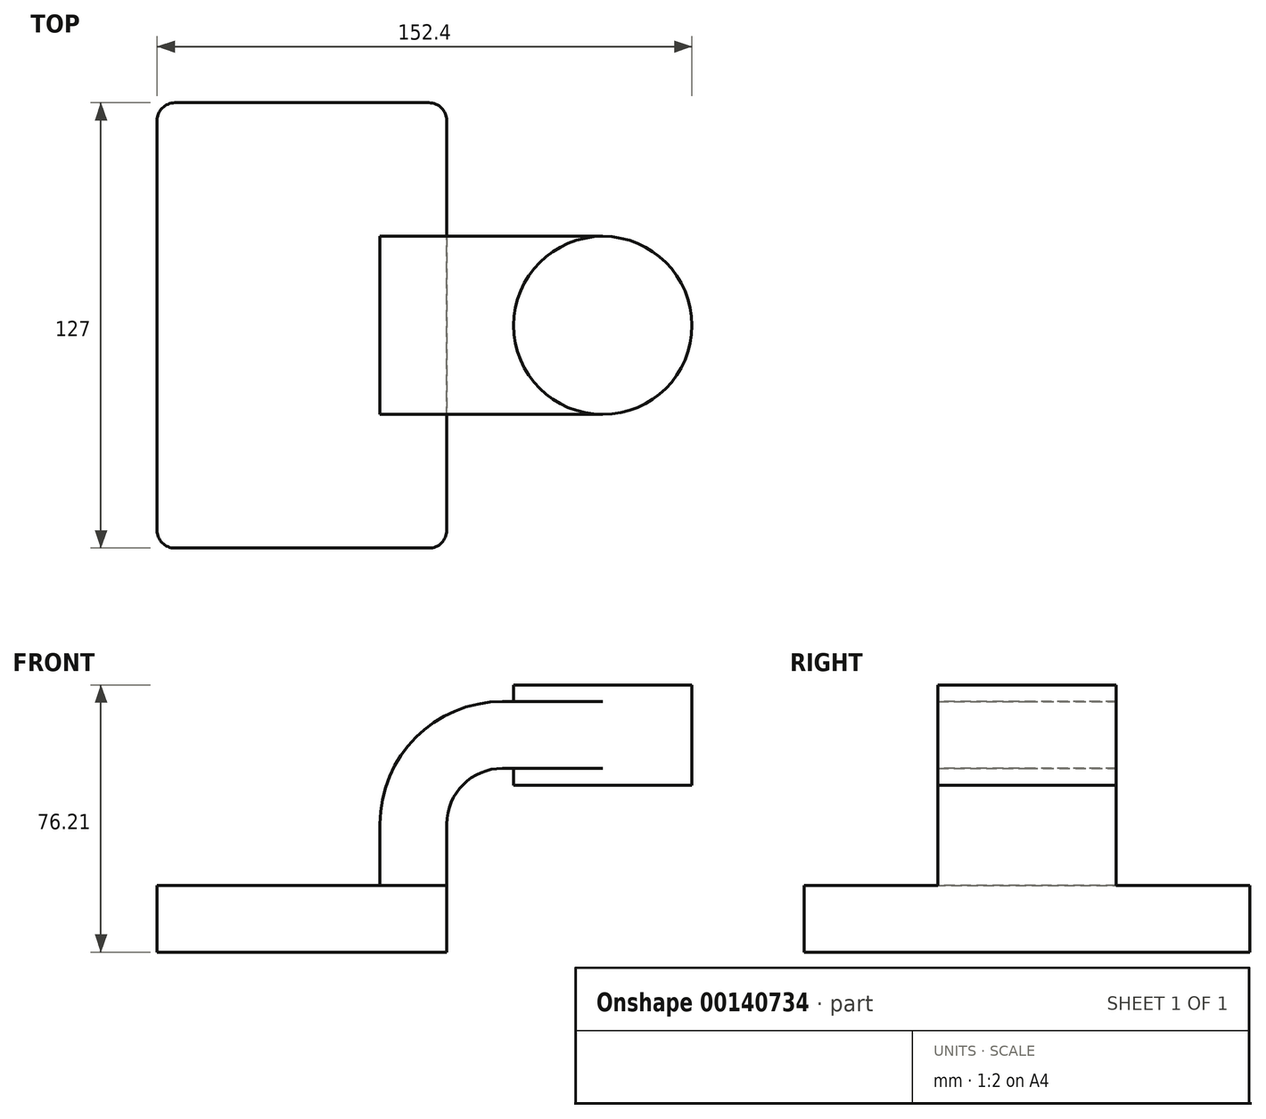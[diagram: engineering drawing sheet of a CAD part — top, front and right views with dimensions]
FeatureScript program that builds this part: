
annotation { "Feature Type Name" : "Feature", "Feature Type Description" : "" }
export const myFeature = defineFeature(function(context is Context, id is Id, definition is map)
    precondition{}
    {
        {
            var Q0;
            Q0=qCreatedBy(makeId("Front.planeOp"),FACE);
            var sketch = newSketch(context, id + "F0", { "sketchPlane" : qUnion([Q0])});
            skLineSegment(sketch, "E0.bottom", {"start": v(-41.28, 9.52) * mm, "end": v(41.27, 9.53) * mm});
            skLineSegment(sketch, "E0.top", {"start": v(-41.28, -9.53) * mm, "end": v(41.28, -9.53) * mm});
            skLineSegment(sketch, "E0.left", {"start": v(-41.28, 9.52) * mm, "end": v(-41.28, -9.53) * mm});
            skLineSegment(sketch, "E0.right", {"start": v(41.27, 9.53) * mm, "end": v(41.28, -9.52) * mm});
            skPoint(sketch, "E0.middle", {"position": v(0, 0) * mm});
            skLineSegment(sketch, "E1.bottom", {"start": v(136.53, 38.1) * mm, "end": v(85.72, 38.1) * mm});
            skLineSegment(sketch, "E1.top", {"start": v(136.53, 66.68) * mm, "end": v(85.72, 66.67) * mm});
            skLineSegment(sketch, "E1.left", {"start": v(136.53, 38.1) * mm, "end": v(136.53, 66.68) * mm});
            skLineSegment(sketch, "E1.right", {"start": v(85.72, 38.1) * mm, "end": v(85.72, 66.67) * mm});
            skPoint(sketch, "E1.middle", {"position": v(111.12, 52.39) * mm});
            skLineSegment(sketch, "E2", {"start": v(41.27, 9.53) * mm, "end": v(41.27, 27) * mm});
            skArc(sketch, "E3", {"start": v(41.27, 27) * mm, "mid": v(45.92, 38.23) * mm, "end": v(57.15, 42.88) * mm});
            skLineSegment(sketch, "E4", {"start": v(57.15, 42.88) * mm, "end": v(111.12, 42.88) * mm});
            skLineSegment(sketch, "E5.0", {"start": v(57.15, 61.93) * mm, "end": v(111.12, 61.93) * mm});
            skArc(sketch, "E5.1", {"start": v(22.22, 27) * mm, "mid": v(32.45, 51.7) * mm, "end": v(57.15, 61.93) * mm});
            skLineSegment(sketch, "E5.2", {"start": v(22.22, 9.53) * mm, "end": v(22.22, 27) * mm});
            skLineSegment(sketch, "E6", {"start": v(111.12, 66.67) * mm, "end": v(111.12, 38.1) * mm});
            skFitSpline(sketch, "E7", {"points": [v(-41.28, 9.52) * mm, v(57.15, 61.93) * mm], "startDerivative": vector(-0.48, 149.14) * mm, "endDerivative": vector(148.6, 0) * mm});
            skSolve(sketch);
        }
        {
            var Q0;
            Q0=makeQuery(id+"F0.imprint","IMPRINT",FACE,{"disambiguationData":[TD([[makeQuery(id+"F0.imprint","IMPRINT",EDGE,{"derivedFrom":sQuery(id+"F0.wireOp",EDGE,"E0.top")}),1.0]])]});
            extrude(context, id + "F1", {"entities" : qUnion([Q0]), "endBound" : BoundingType.SYMMETRIC, "depth" : 127 * mm});
        }
        {
            var Q0;
            Q0=makeQuery(id+"F0.imprint","IMPRINT",FACE,{"disambiguationData":[TD([[makeQuery(id+"F0.imprint","IMPRINT",EDGE,{"derivedFrom":sQuery(id+"F0.wireOp",EDGE,"E0.top")}),1.0]])]});
            var Q1;
            {var subQ2=sQuery(id+"F0.wireOp",EDGE,"E2");Q1=makeQuery(id+"F0.imprint","IMPRINT",FACE,{"disambiguationData":[TD([[makeQuery(id+"F0.imprint","IMPRINT",EDGE,{"derivedFrom":subQ2}),1.0]])]});}
            var Q2;
            Q2 = qConstructionFilter(qBodyType(qCreatedBy(id + "F0" ,EDGE), BodyType.WIRE), ConstructionObject.NO);
            extrude(context, id + "F2", {"entities" : qUnion([Q0, Q1]), "operationType" : NewBodyOperationType.ADD, "surfaceEntities" : qUnion([Q2]), "endBound" : BoundingType.SYMMETRIC, "oppositeDirection" : true, "depth" : 50.8 * mm});
        }
        {
            var Q0;
            Q0=makeQuery(id+"F0.imprint","IMPRINT",FACE,{"disambiguationData":[TD([[makeQuery(id+"F0.imprint","IMPRINT",EDGE,{"derivedFrom":sQuery(id+"F0.wireOp",EDGE,"E5.1")}),1.0]])]});
            extrude(context, id + "F3", {"entities" : qUnion([Q0]), "operationType" : NewBodyOperationType.ADD, "endBound" : BoundingType.SYMMETRIC, "depth" : 20.95 * mm});
        }
        {
            var Q0;
            {var subQ0=sQuery(id+"F0.wireOp",EDGE,"E1.right");var subQ1=sQuery(id+"F0.wireOp",EDGE,"E1.bottom");var subQ2=makeQuery(id+"F0.imprint","INTERSECT",VERTEX,{"derivedFrom":[subQ1,subQ0]});Q0=makeQuery(id+"F0.imprint","IMPRINT",FACE,{"disambiguationData":[TD([[makeQuery(id+"F0.imprint","IMPRINT",EDGE,{"disambiguationData":[TD([[subQ2,1.0]])],"derivedFrom":subQ1}),-1.0]])]});}
            var Q1;
            {var subQ0=sQuery(id+"F0.wireOp",EDGE,"E4");var subQ1=sQuery(id+"F0.wireOp",EDGE,"E1.right");var subQ2=makeQuery(id+"F0.imprint","INTERSECT",VERTEX,{"derivedFrom":[subQ1,subQ0]});Q1=makeQuery(id+"F0.imprint","IMPRINT",FACE,{"disambiguationData":[TD([[makeQuery(id+"F0.imprint","IMPRINT",EDGE,{"disambiguationData":[TD([[subQ2,-1.0]])],"derivedFrom":subQ1}),-1.0]])]});}
            var Q2;
            {var subQ0=sQuery(id+"F0.wireOp",EDGE,"E1.right");var subQ1=sQuery(id+"F0.wireOp",EDGE,"E1.top");var subQ2=makeQuery(id+"F0.imprint","INTERSECT",VERTEX,{"derivedFrom":[subQ1,subQ0]});Q2=makeQuery(id+"F0.imprint","IMPRINT",FACE,{"disambiguationData":[TD([[makeQuery(id+"F0.imprint","IMPRINT",EDGE,{"disambiguationData":[TD([[subQ2,1.0]])],"derivedFrom":subQ1}),1.0]])]});}
            var Q3;
            Q3=sQuery(id+"F0.wireOp",EDGE,"E1.right");
            revolve(context, id + "F4", {"operationType" : NewBodyOperationType.ADD, "entities" : qUnion([Q0, Q1, Q2]), "axis" : qUnion([Q3]), "revolveType" : RevolveType.FULL});
        }
        {
            var Q0;
            Q0=makeQuery(id+"F1.opExtrude","CAP_EDGE",EDGE,{"disambiguationData":[OSD([sQuery(id+"F0.wireOp",EDGE,"E0.right")])],"isStart":true});
            var Q1;
            Q1=makeQuery(id+"F1.opExtrude","CAP_EDGE",EDGE,{"disambiguationData":[OSD([sQuery(id+"F0.wireOp",EDGE,"E0.left")])],"isStart":true});
            var Q2;
            Q2=makeQuery(id+"F1.opExtrude","CAP_EDGE",EDGE,{"disambiguationData":[OSD([sQuery(id+"F0.wireOp",EDGE,"E0.left")])],"isStart":false});
            var Q3;
            Q3=makeQuery(id+"F1.opExtrude","CAP_EDGE",EDGE,{"disambiguationData":[OSD([sQuery(id+"F0.wireOp",EDGE,"E0.right")])],"isStart":false});
            fillet(context, id + "F5", {"entities" : qUnion([Q0, Q1, Q2, Q3]), "radius" : 5.08 * mm, "tangentPropagation" : true, "allowEdgeOverflow" : false});
        }
    });
